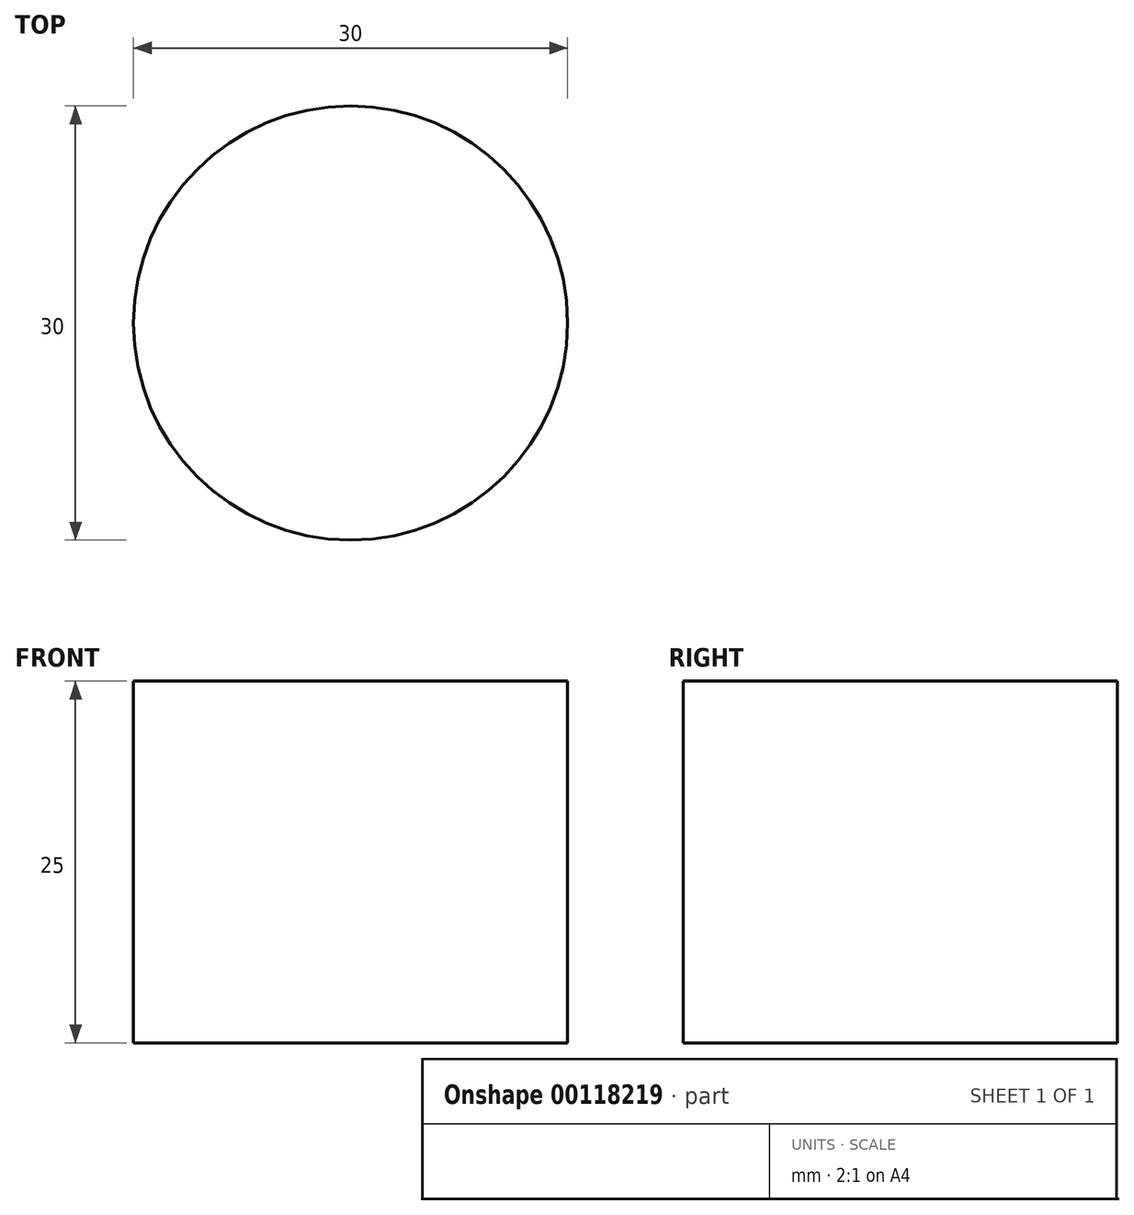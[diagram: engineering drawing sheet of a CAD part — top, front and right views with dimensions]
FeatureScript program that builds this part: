
annotation { "Feature Type Name" : "Feature", "Feature Type Description" : "" }
export const myFeature = defineFeature(function(context is Context, id is Id, definition is map)
    precondition{}
    {
        {
            var Q0;
            Q0=qCreatedBy(makeId("Top.planeOp"),FACE);
            var sketch = newSketch(context, id + "F0", { "sketchPlane" : qUnion([Q0])});
            skCircle(sketch, "E0", {"center": v(0, 0) * mm, "radius": 15 * mm});
            skSolve(sketch);
        }
        {
            var Q0;
            Q0=makeQuery(id+"F0.imprint","IMPRINT",FACE,{"disambiguationData":[TD([[makeQuery(id+"F0.imprint","IMPRINT",EDGE,{"derivedFrom":sQuery(id+"F0.wireOp",EDGE,"E0")}),1.0]])]});
            extrude(context, id + "F1", {"entities" : qUnion([Q0]), "depth" : 25 * mm});
        }
    });
